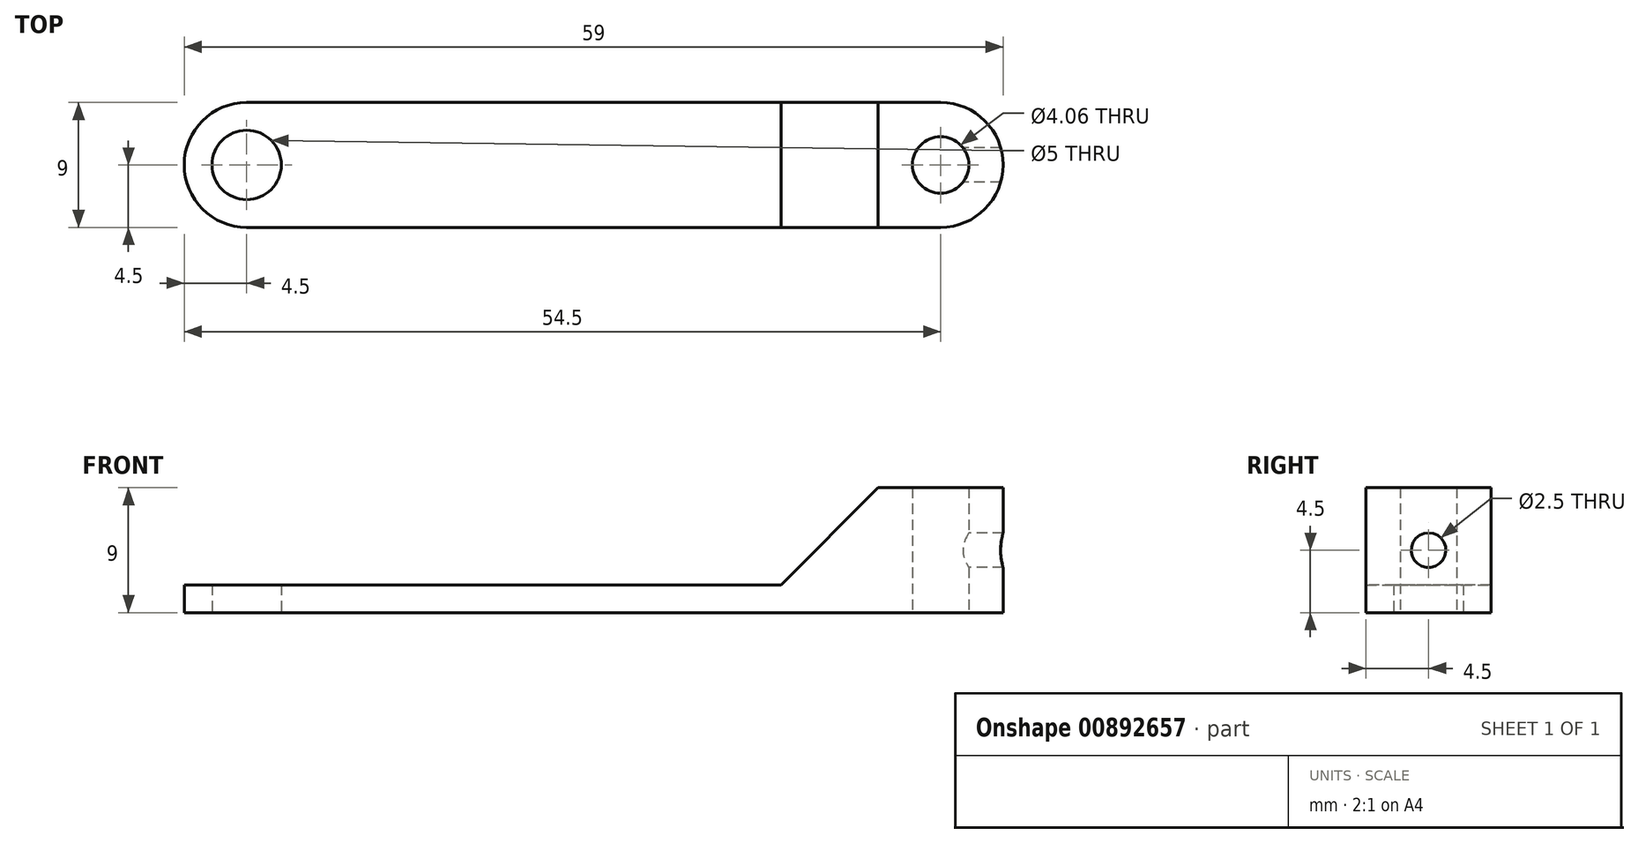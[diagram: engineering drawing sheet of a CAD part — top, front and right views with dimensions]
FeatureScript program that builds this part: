
annotation { "Feature Type Name" : "Feature", "Feature Type Description" : "" }
export const myFeature = defineFeature(function(context is Context, id is Id, definition is map)
    precondition{}
    {
        {
            var Q0;
            Q0=qCreatedBy(makeId("Top.planeOp"),FACE);
            var sketch = newSketch(context, id + "F0", { "sketchPlane" : qUnion([Q0])});
            skCircle(sketch, "E0", {"center": v(0, 0) * mm, "radius": 2.03 * mm});
            skCircle(sketch, "E1", {"center": v(-50, 0) * mm, "radius": 2.5 * mm});
            skLineSegment(sketch, "E2", {"start": v(-50, 4.5) * mm, "end": v(0, 4.5) * mm});
            skLineSegment(sketch, "E3", {"start": v(-50, -4.5) * mm, "end": v(0, -4.5) * mm});
            skArc(sketch, "E4", {"start": v(-50, 4.5) * mm, "mid": v(-54.5, 0) * mm, "end": v(-50, -4.5) * mm});
            skArc(sketch, "E5", {"start": v(0, -4.5) * mm, "mid": v(4.5, 0) * mm, "end": v(0, 4.5) * mm});
            skSolve(sketch);
        }
        {
            var Q0;
            Q0=makeQuery(id+"F0.imprint","IMPRINT",FACE,{"disambiguationData":[TD([[makeQuery(id+"F0.imprint","IMPRINT",EDGE,{"derivedFrom":sQuery(id+"F0.wireOp",EDGE,"E0")}),-1.0]])]});
            extrude(context, id + "F1", {"entities" : qUnion([Q0]), "depth" : 9 * mm, "offsetDistance" : 25.4 * mm});
        }
        {
            var Q0;
            Q0=makeQuery(id+"F1.opExtrude","SWEPT_FACE",FACE,{"disambiguationData":[OSD([sQuery(id+"F0.wireOp",EDGE,"E3")])]});
            var sketch = newSketch(context, id + "F2", { "sketchPlane" : qUnion([Q0])});
            skLineSegment(sketch, "E6", {"start": v(-94.76, 2) * mm, "end": v(-11.5, 2) * mm});
            skLineSegment(sketch, "E7", {"start": v(-11.5, 2) * mm, "end": v(-4.5, 9) * mm});
            skLineSegment(sketch, "E8", {"start": v(-4.5, 9) * mm, "end": v(-98.53, 9) * mm});
            skLineSegment(sketch, "E9", {"start": v(-98.53, 9) * mm, "end": v(-94.76, 2) * mm});
            skSolve(sketch);
        }
        {
            var Q0;
            Q0 = qSketchRegion(id + "F2", true);
            extrude(context, id + "F3", {"entities" : qUnion([Q0]), "operationType" : NewBodyOperationType.REMOVE, "endBound" : BoundingType.THROUGH_ALL, "oppositeDirection" : true, "depth" : 25.4 * mm, "offsetDistance" : 25.4 * mm});
        }
        {
            var Q0;
            Q0=qCreatedBy(makeId("Right.planeOp"),FACE);
            var sketch = newSketch(context, id + "F4", { "sketchPlane" : qUnion([Q0])});
            skCircle(sketch, "E10", {"center": v(0, 4.5) * mm, "radius": 1.25 * mm});
            skSolve(sketch);
        }
        {
            var Q0;
            Q0 = qSketchRegion(id + "F4", true);
            extrude(context, id + "F5", {"entities" : qUnion([Q0]), "operationType" : NewBodyOperationType.REMOVE, "endBound" : BoundingType.THROUGH_ALL, "depth" : 25.4 * mm, "offsetDistance" : 25.4 * mm});
        }
    });
